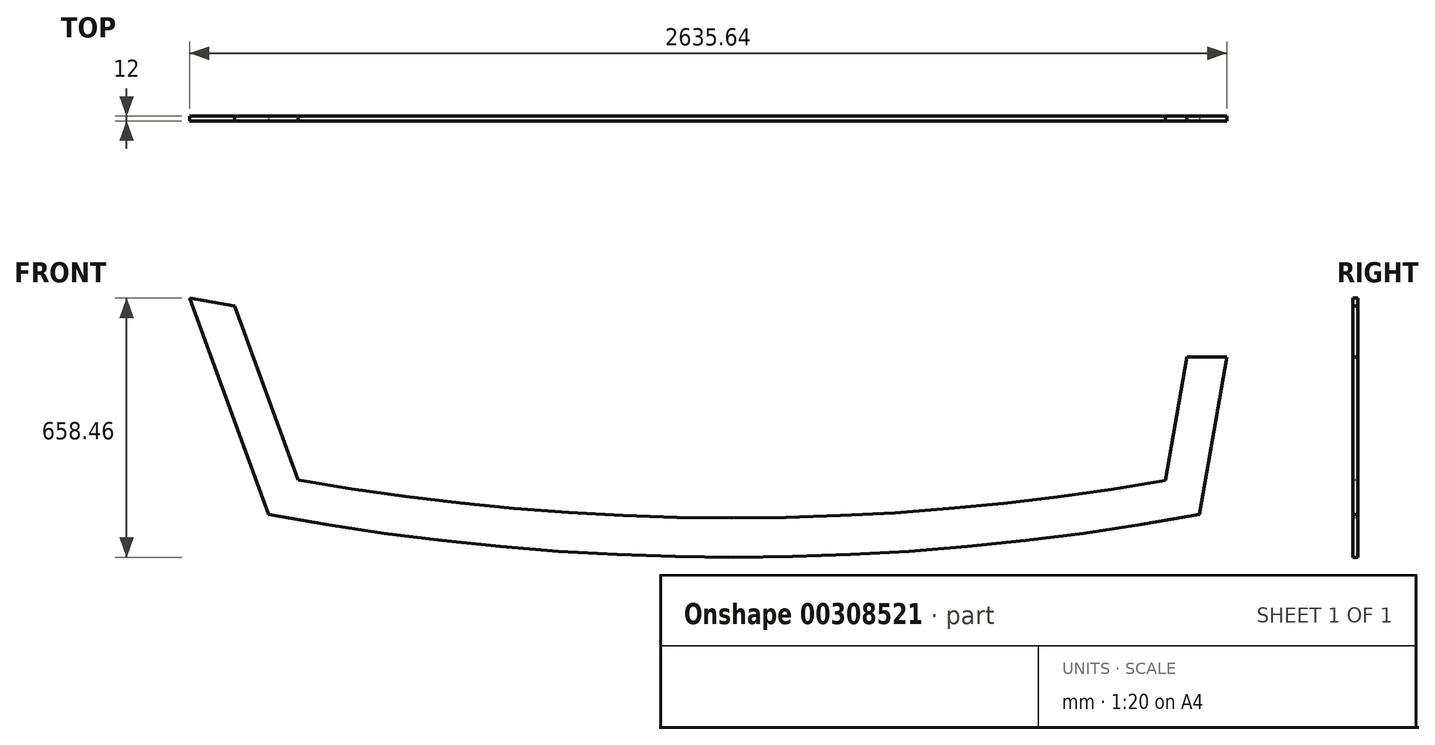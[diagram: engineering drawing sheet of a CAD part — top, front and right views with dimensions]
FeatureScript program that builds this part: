
annotation { "Feature Type Name" : "Feature", "Feature Type Description" : "" }
export const myFeature = defineFeature(function(context is Context, id is Id, definition is map)
    precondition{}
    {
        {
            var Q0;
            Q0=qCreatedBy(makeId("Top.planeOp"),FACE);
            var sketch = newSketch(context, id + "F0", { "sketchPlane" : qUnion([Q0])});
            skLineSegment(sketch, "E0", {"start": v(-1250, 0) * mm, "end": v(1250, 0) * mm});
            skPoint(sketch, "E1", {"position": v(0, 0) * mm});
            skLineSegment(sketch, "E2", {"start": v(250, 325) * mm, "end": v(250, -325) * mm});
            skPoint(sketch, "E3", {"position": v(250, 0) * mm});
            skLineSegment(sketch, "E4", {"start": v(-1250, 6) * mm, "end": v(-1250, -6) * mm});
            skPoint(sketch, "E5", {"position": v(-1250, 0) * mm});
            skLineSegment(sketch, "E6", {"start": v(1250, -6) * mm, "end": v(1250, 6) * mm});
            skPoint(sketch, "E7", {"position": v(1250, 0) * mm});
            skLineSegment(sketch, "E8", {"start": v(-250, 300) * mm, "end": v(-250, -300) * mm});
            skPoint(sketch, "E9", {"position": v(-250, 0) * mm});
            skArc(sketch, "E10", {"start": v(-250, 300) * mm, "mid": v(-762.11, 194.2) * mm, "end": v(-1250, 6) * mm});
            skArc(sketch, "E11", {"start": v(-1250, -6) * mm, "mid": v(-762.11, -194.2) * mm, "end": v(-250, -300) * mm});
            skArc(sketch, "E12", {"start": v(250, 325) * mm, "mid": v(-0.45, 321.45) * mm, "end": v(-250, 300) * mm});
            skArc(sketch, "E13", {"start": v(1250, 6) * mm, "mid": v(773.06, 237.8) * mm, "end": v(250, 325) * mm});
            skArc(sketch, "E14", {"start": v(-250, -300) * mm, "mid": v(-0.45, -321.45) * mm, "end": v(250, -325) * mm});
            skArc(sketch, "E15", {"start": v(250, -325) * mm, "mid": v(773.06, -237.8) * mm, "end": v(1250, -6) * mm});
            skLineSegment(sketch, "E16", {"start": v(-900, 150.23) * mm, "end": v(-900, -150.23) * mm});
            skLineSegment(sketch, "E17", {"start": v(-550, 248.7) * mm, "end": v(-550, -248.7) * mm});
            skLineSegment(sketch, "E18", {"start": v(0, 321.47) * mm, "end": v(0, -321.47) * mm});
            skLineSegment(sketch, "E19", {"start": v(550, 293.96) * mm, "end": v(550, -293.96) * mm});
            skLineSegment(sketch, "E20", {"start": v(900, 192.14) * mm, "end": v(900, -192.14) * mm});
            skSolve(sketch);
        }
        {
            var Q0;
            Q0=qCreatedBy(makeId("Front.planeOp"),FACE);
            var sketch = newSketch(context, id + "F1", { "sketchPlane" : qUnion([Q0])});
            skLineSegment(sketch, "E21", {"start": v(-1359.2, 300) * mm, "end": v(-1159, -250) * mm});
            skLineSegment(sketch, "E22", {"start": v(1276.45, 150) * mm, "end": v(1205.92, -250) * mm});
            skArc(sketch, "E23", {"start": v(-1159, -250) * mm, "mid": v(23.46, -358.46) * mm, "end": v(1205.92, -250) * mm});
            skLineSegment(sketch, "E24.0", {"start": v(-1244.9, 279.85) * mm, "end": v(-1084.13, -161.9) * mm});
            skArc(sketch, "E25.1", {"start": v(-1084.13, -161.9) * mm, "mid": v(17.63, -258.46) * mm, "end": v(1119.56, -163.9) * mm});
            skLineSegment(sketch, "E26.0", {"start": v(1174.9, 150) * mm, "end": v(1119.56, -163.9) * mm});
            skLineSegment(sketch, "E27", {"start": v(1276.45, 150) * mm, "end": v(1174.9, 150) * mm});
            skLineSegment(sketch, "E28", {"start": v(-1359.2, 300) * mm, "end": v(-1244.9, 279.85) * mm});
            skLineSegment(sketch, "E29", {"start": v(-1159, -250) * mm, "end": v(-1084.13, -161.9) * mm});
            skLineSegment(sketch, "E30", {"start": v(1205.92, -250) * mm, "end": v(1119.56, -163.9) * mm});
            skSolve(sketch);
        }
        {
            var Q0;
            Q0=makeQuery(id+"F1.imprint","IMPRINT",FACE,{"disambiguationData":[TD([[makeQuery(id+"F1.imprint","IMPRINT",EDGE,{"derivedFrom":sQuery(id+"F1.wireOp",EDGE,"E23")}),1.0]])]});
            var Q1;
            Q1=makeQuery(id+"F1.imprint","IMPRINT",FACE,{"disambiguationData":[TD([[makeQuery(id+"F1.imprint","IMPRINT",EDGE,{"derivedFrom":sQuery(id+"F1.wireOp",EDGE,"E21")}),1.0]])]});
            var Q2;
            Q2=makeQuery(id+"F1.imprint","IMPRINT",FACE,{"disambiguationData":[TD([[makeQuery(id+"F1.imprint","IMPRINT",EDGE,{"derivedFrom":sQuery(id+"F1.wireOp",EDGE,"E22")}),-1.0]])]});
            extrude(context, id + "F2", {"entities" : qUnion([Q0, Q1, Q2]), "endBound" : BoundingType.SYMMETRIC, "oppositeDirection" : true, "depth" : 12 * mm, "offsetDistance" : 25 * mm});
        }
        {
            var Q0;
            Q0=sQuery(id+"F0.wireOp",EDGE,"E16");
            cPlane(context, id + "F3", {"entities" : qUnion([Q0]), "cplaneType" : CPlaneType.LINE_ANGLE, "offset" : 25 * mm, "angle" : 90 * degree, "width" : 150 * mm, "height" : 150 * mm});
        }
    });
